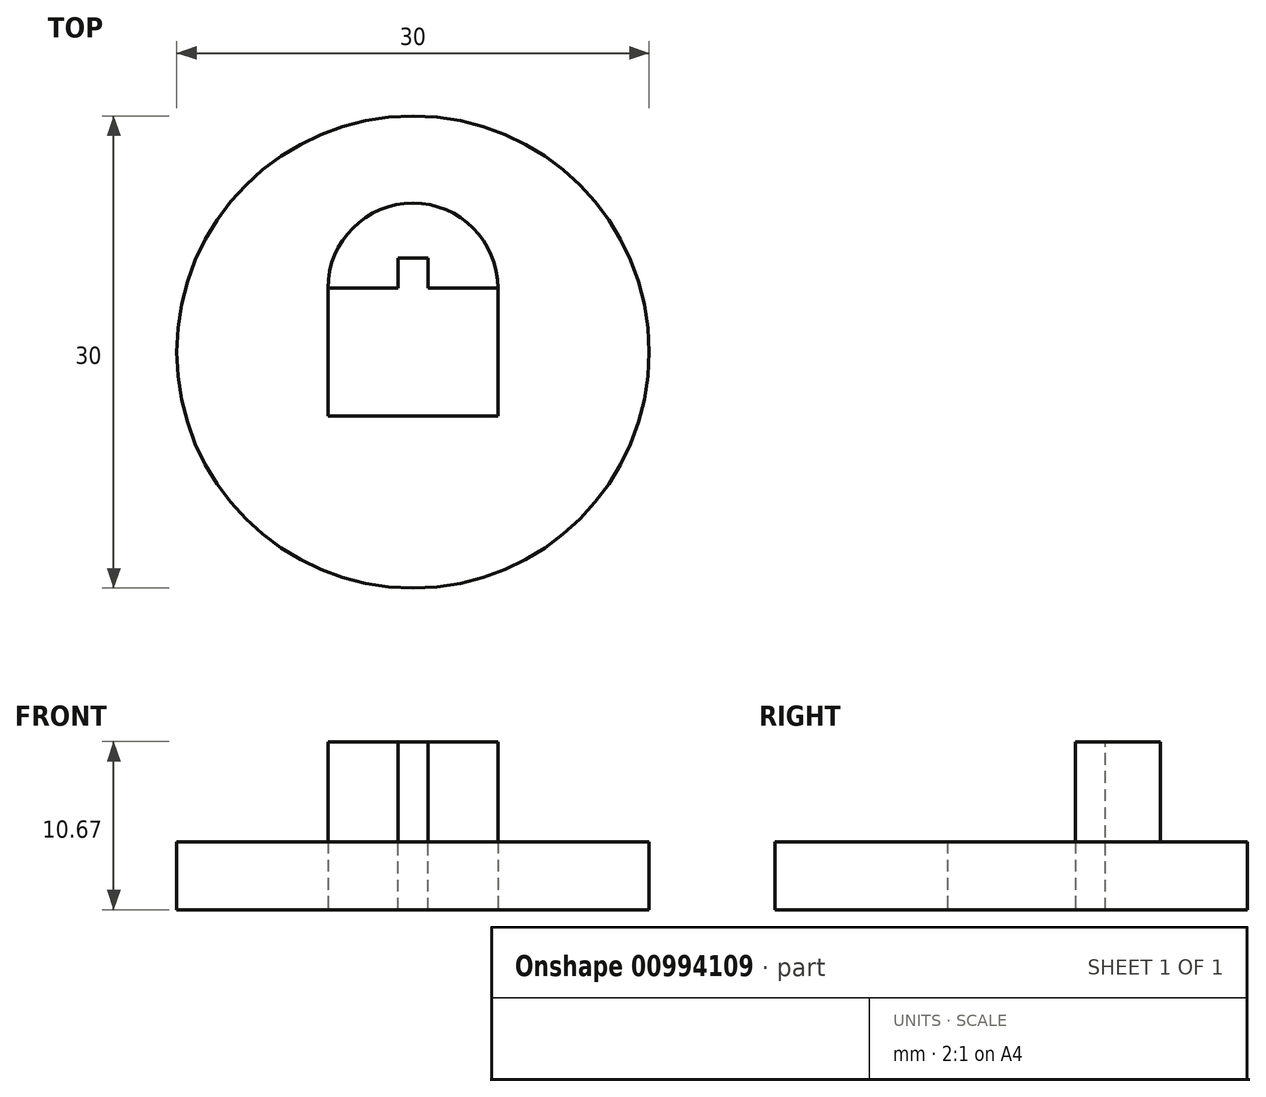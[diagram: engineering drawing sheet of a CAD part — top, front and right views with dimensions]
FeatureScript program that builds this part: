
annotation { "Feature Type Name" : "Feature", "Feature Type Description" : "" }
export const myFeature = defineFeature(function(context is Context, id is Id, definition is map)
    precondition{}
    {
        {
            var Q0;
            Q0=qCreatedBy(makeId("Top.planeOp"),FACE);
            var sketch = newSketch(context, id + "F0", { "sketchPlane" : qUnion([Q0])});
            skCircle(sketch, "E0", {"center": v(0, 0) * mm, "radius": 15 * mm});
            skLineSegment(sketch, "E1.bottom", {"start": v(5.4, -4.06) * mm, "end": v(-5.4, -4.06) * mm});
            skLineSegment(sketch, "E1.top", {"start": v(5.4, 4.06) * mm, "end": v(-5.4, 4.06) * mm});
            skLineSegment(sketch, "E1.left", {"start": v(5.4, -4.06) * mm, "end": v(5.4, 4.06) * mm});
            skLineSegment(sketch, "E1.right", {"start": v(-5.4, -4.06) * mm, "end": v(-5.4, 4.06) * mm});
            skSolve(sketch);
        }
        {
            var Q0;
            Q0=makeQuery(id+"F0.imprint","IMPRINT",FACE,{"disambiguationData":[TD([[makeQuery(id+"F0.imprint","IMPRINT",EDGE,{"derivedFrom":sQuery(id+"F0.wireOp",EDGE,"E0")}),1.0]])]});
            extrude(context, id + "F1", {"entities" : qUnion([Q0]), "depth" : 4.32 * mm, "offsetDistance" : 25.4 * mm});
        }
        {
            var Q0;
            Q0=makeQuery(id+"F1.opExtrude","CAP_FACE",FACE,{"disambiguationData":[OSD([sQuery(id+"F0.wireOp",EDGE,"E0"),sQuery(id+"F0.wireOp",EDGE,"E1.bottom"),sQuery(id+"F0.wireOp",EDGE,"E1.top"),sQuery(id+"F0.wireOp",EDGE,"E1.left"),sQuery(id+"F0.wireOp",EDGE,"E1.right")])],"isStart":false});
            var sketch = newSketch(context, id + "F2", { "sketchPlane" : qUnion([Q0])});
            skLineSegment(sketch, "E2.bottom", {"start": v(0.95, 4.06) * mm, "end": v(-0.95, 4.06) * mm});
            skLineSegment(sketch, "E2.top", {"start": v(0.95, 5.97) * mm, "end": v(-0.95, 5.97) * mm});
            skLineSegment(sketch, "E2.left", {"start": v(0.95, 4.06) * mm, "end": v(0.95, 5.97) * mm});
            skLineSegment(sketch, "E2.right", {"start": v(-0.95, 4.06) * mm, "end": v(-0.95, 5.97) * mm});
            skPoint(sketch, "E3", {"position": v(0, 5.97) * mm});
            skSolve(sketch);
        }
        {
            var Q0;
            Q0 = qSketchRegion(id + "F2", true);
            extrude(context, id + "F3", {"entities" : qUnion([Q0]), "operationType" : NewBodyOperationType.REMOVE, "oppositeDirection" : true, "depth" : 25.4 * mm, "offsetDistance" : 25.4 * mm});
        }
        {
            var Q0;
            Q0=makeQuery(id+"F1.opExtrude","CAP_FACE",FACE,{"disambiguationData":[OSD([sQuery(id+"F0.wireOp",EDGE,"E0"),sQuery(id+"F0.wireOp",EDGE,"E1.bottom"),sQuery(id+"F0.wireOp",EDGE,"E1.top"),sQuery(id+"F0.wireOp",EDGE,"E1.left"),sQuery(id+"F0.wireOp",EDGE,"E1.right")])],"isStart":false});
            var sketch = newSketch(context, id + "F4", { "sketchPlane" : qUnion([Q0])});
            skArc(sketch, "E4", {"start": v(5.4, 4.06) * mm, "mid": v(0, 9.46) * mm, "end": v(-5.4, 4.06) * mm});
            skLineSegment(sketch, "E5", {"start": v(-0.95, 4.06) * mm, "end": v(0.95, 4.06) * mm, "construction": true});
            skLineSegment(sketch, "E6", {"start": v(-0.95, 4.06) * mm, "end": v(-5.4, 4.06) * mm});
            skLineSegment(sketch, "E7", {"start": v(0.95, 4.06) * mm, "end": v(5.4, 4.06) * mm});
            skLineSegment(sketch, "E8", {"start": v(0.95, 4.06) * mm, "end": v(0.95, 5.97) * mm});
            skLineSegment(sketch, "E9", {"start": v(0.95, 5.97) * mm, "end": v(-0.95, 5.97) * mm});
            skLineSegment(sketch, "E10", {"start": v(-0.95, 5.97) * mm, "end": v(-0.95, 4.06) * mm});
            skSolve(sketch);
        }
        {
            var Q0;
            Q0 = qSketchRegion(id + "F4", true);
            extrude(context, id + "F5", {"entities" : qUnion([Q0]), "operationType" : NewBodyOperationType.ADD, "depth" : 6.35 * mm, "offsetDistance" : 25.4 * mm});
        }
    });
